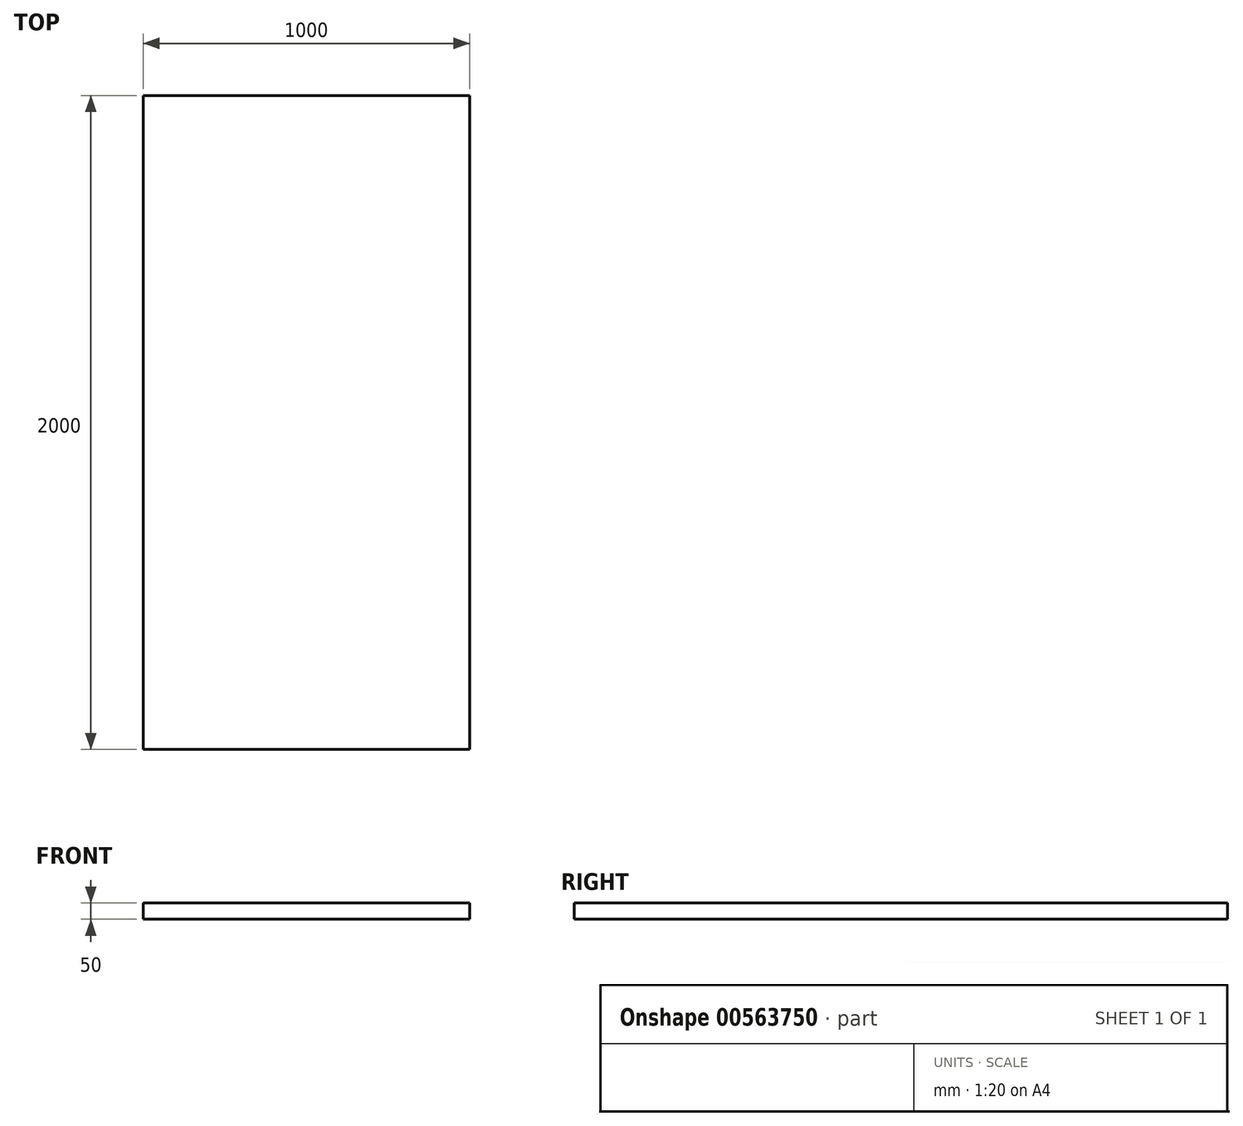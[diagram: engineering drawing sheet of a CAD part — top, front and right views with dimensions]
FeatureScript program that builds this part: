
annotation { "Feature Type Name" : "Feature", "Feature Type Description" : "" }
export const myFeature = defineFeature(function(context is Context, id is Id, definition is map)
    precondition{}
    {
        {
            var Q0;
            Q0=qCreatedBy(makeId("Top.planeOp"),FACE);
            var sketch = newSketch(context, id + "F0", { "sketchPlane" : qUnion([Q0])});
            skLineSegment(sketch, "E0.bottom", {"start": v(-511.88, 1129.65) * mm, "end": v(488.12, 1129.65) * mm});
            skLineSegment(sketch, "E0.top", {"start": v(-511.88, -870.35) * mm, "end": v(488.12, -870.35) * mm});
            skLineSegment(sketch, "E0.left", {"start": v(-511.88, 1129.65) * mm, "end": v(-511.88, -870.35) * mm});
            skLineSegment(sketch, "E0.right", {"start": v(488.12, 1129.65) * mm, "end": v(488.12, -870.35) * mm});
            skSolve(sketch);
        }
        {
            var Q0;
            Q0=makeQuery(id+"F0.imprint","IMPRINT",FACE,{"disambiguationData":[TD([[makeQuery(id+"F0.imprint","IMPRINT",EDGE,{"derivedFrom":sQuery(id+"F0.wireOp",EDGE,"E0.bottom")}),-1.0]])]});
            extrude(context, id + "F1", {"entities" : qUnion([Q0]), "depth" : 50 * mm, "offsetDistance" : 25 * mm});
        }
    });
